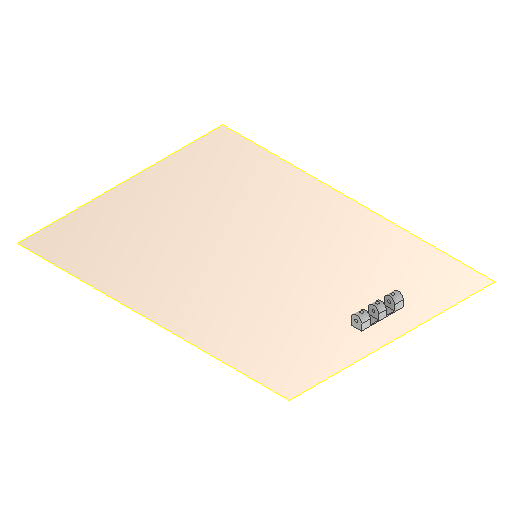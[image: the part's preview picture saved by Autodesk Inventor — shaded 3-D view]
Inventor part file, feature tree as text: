
AUTODESK INVENTOR PART (.ipt)
format: ipt  version: 2024.1 (Build 281209000, 209)  size: 193,024 bytes
history: native  units: mm
features: extrude x3, sketch x3, other x2, plane x1, fillet x1, reference x1, projected_geometry x1
ambient origin geometry x8: Origin, YZ Plane, XZ Plane, XY Plane, X Axis, Y Axis, Z Axis, Center Point
bodies: Volumenkörper1 (feature_tree)
feature tree (12):
  plane  "Arbeitsebene1"
  extrude  "Extrusion1"  Depth=10.0mm
  fillet  "Rundung1"  Radius=50.0mm
  extrude  "Extrusion2"  Depth=5.0mm
  extrude  "Extrusion3"  Depth=10.0mm
  sketch  "Skizze1"  dims[d0=10.0mm d1=40.0mm d2=50.0mm d3=0.0mm]
  reference  "Referenz1"
  sketch  "Skizze2"  dims[d4=5.0mm d5=6.0mm]
  projected_geometry  "Projizierte Kontur1"
  sketch  "Skizze3"  dims[d6=0.0mm d7=0.0mm d8=2.8mm d9=10.0mm d10=8.0mm d11=10.0mm d12=8.0mm d13=2.0mm d14=2.2mm d15=10.0mm d16=0.0mm]
  other  "Assembly_Planktoscope_Uc2version_wormdrive_V3.iam"
  other  "60_Planktoscope_MicroscopeHolder_Bottom_v0:1"
